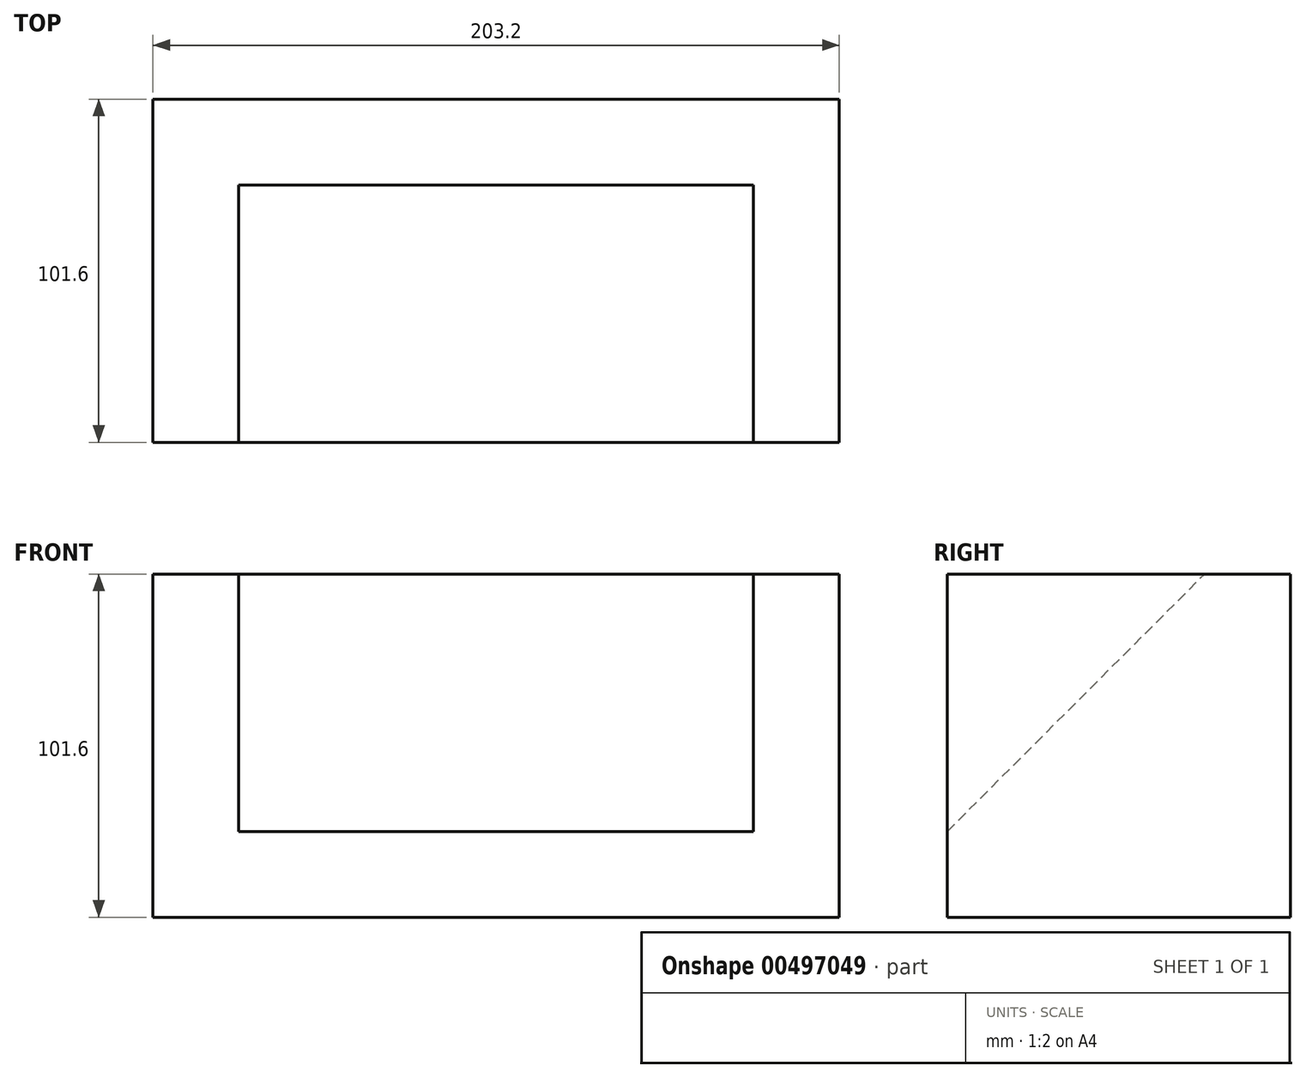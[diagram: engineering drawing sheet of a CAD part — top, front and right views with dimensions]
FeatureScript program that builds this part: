
annotation { "Feature Type Name" : "Feature", "Feature Type Description" : "" }
export const myFeature = defineFeature(function(context is Context, id is Id, definition is map)
    precondition{}
    {
        {
            var Q0;
            Q0=qCreatedBy(makeId("Front.planeOp"),FACE);
            var sketch = newSketch(context, id + "F0", { "sketchPlane" : qUnion([Q0])});
            skLineSegment(sketch, "E0", {"start": v(-69.7, -45.35) * mm, "end": v(133.5, -45.35) * mm});
            skLineSegment(sketch, "E1", {"start": v(133.5, -45.35) * mm, "end": v(133.5, 56.25) * mm});
            skLineSegment(sketch, "E2", {"start": v(133.5, 56.25) * mm, "end": v(-69.7, 56.25) * mm});
            skLineSegment(sketch, "E3", {"start": v(-69.7, 56.25) * mm, "end": v(-69.7, -45.35) * mm});
            skSolve(sketch);
        }
        {
            var Q0;
            Q0=makeQuery(id+"F0.imprint","IMPRINT",FACE,{"disambiguationData":[TD([[makeQuery(id+"F0.imprint","IMPRINT",EDGE,{"derivedFrom":sQuery(id+"F0.wireOp",EDGE,"E0")}),1.0]])]});
            extrude(context, id + "F1", {"entities" : qUnion([Q0]), "depth" : 101.6 * mm});
        }
        {
            var Q0;
            Q0=makeQuery(id+"F1.opExtrude","SWEPT_FACE",FACE,{"disambiguationData":[OSD([sQuery(id+"F0.wireOp",EDGE,"E2")])]});
            var sketch = newSketch(context, id + "F2", { "sketchPlane" : qUnion([Q0])});
            skLineSegment(sketch, "E4", {"start": v(133.5, -101.6) * mm, "end": v(108.1, -101.6) * mm});
            skLineSegment(sketch, "E5", {"start": v(108.1, -101.6) * mm, "end": v(108.1, -25.4) * mm});
            skLineSegment(sketch, "E6", {"start": v(108.1, -25.4) * mm, "end": v(-44.3, -25.4) * mm});
            skLineSegment(sketch, "E7", {"start": v(-44.3, -25.4) * mm, "end": v(-44.3, -101.6) * mm});
            skLineSegment(sketch, "E8", {"start": v(-44.3, -101.6) * mm, "end": v(-69.7, -101.6) * mm});
            skSolve(sketch);
        }
        {
            var Q0;
            {var subQ0=sQuery(id+"F2.wireOp",EDGE,"E5");Q0=makeQuery(id+"F2.imprint","IMPRINT",FACE,{"disambiguationData":[TD([[makeQuery(id+"F2.imprint","IMPRINT",EDGE,{"derivedFrom":subQ0}),1.0]])]});}
            extrude(context, id + "F3", {"entities" : qUnion([Q0]), "operationType" : NewBodyOperationType.REMOVE, "oppositeDirection" : true, "depth" : 76.2 * mm});
        }
        {
            var Q0;
            Q0=makeQuery(id+"F3.boolean.opBoolean","COPY",FACE,{"derivedFrom":makeQuery(id+"F3.opExtrude","SWEPT_FACE",FACE,{"disambiguationData":[OSD([sQuery(id+"F2.wireOp",EDGE,"E7")])]})});
            var sketch = newSketch(context, id + "F4", { "sketchPlane" : qUnion([Q0])});
            skLineSegment(sketch, "E9", {"start": v(-101.6, -19.95) * mm, "end": v(-25.4, 56.25) * mm});
            skLineSegment(sketch, "E10", {"start": v(-25.4, 56.25) * mm, "end": v(-25.4, -19.95) * mm});
            skLineSegment(sketch, "E11", {"start": v(-25.4, -19.95) * mm, "end": v(-101.6, -19.95) * mm});
            skSolve(sketch);
        }
        {
            var Q0;
            Q0=makeQuery(id+"F4.imprint","IMPRINT",FACE,{"disambiguationData":[TD([[makeQuery(id+"F4.imprint","IMPRINT",EDGE,{"derivedFrom":sQuery(id+"F4.wireOp",EDGE,"E9")}),-1.0]])]});
            extrude(context, id + "F5", {"entities" : qUnion([Q0]), "operationType" : NewBodyOperationType.ADD, "depth" : 152.4 * mm});
        }
    });
